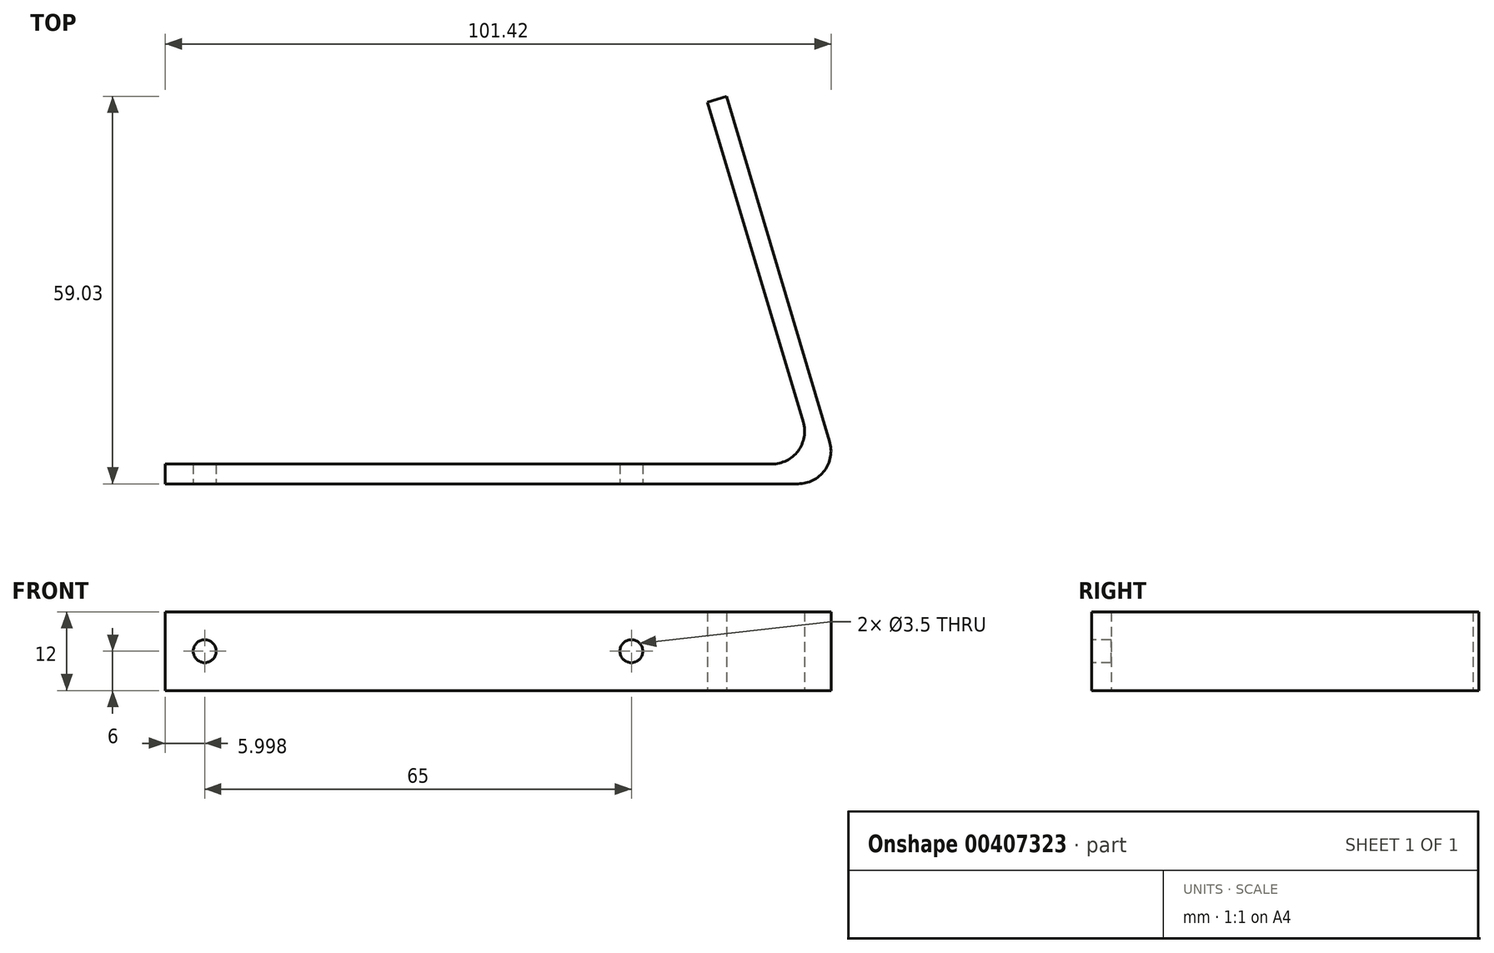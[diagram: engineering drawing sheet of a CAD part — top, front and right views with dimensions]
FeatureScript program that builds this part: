
annotation { "Feature Type Name" : "Feature", "Feature Type Description" : "" }
export const myFeature = defineFeature(function(context is Context, id is Id, definition is map)
    precondition{}
    {
        {
            var Q0;
            Q0=qCreatedBy(makeId("Top.planeOp"),FACE);
            var sketch = newSketch(context, id + "F0", { "sketchPlane" : qUnion([Q0])});
            skLineSegment(sketch, "E0.bottom", {"start": v(-64.62, -2.8) * mm, "end": v(27.77, -2.8) * mm});
            skLineSegment(sketch, "E0.top", {"start": v(-64.62, -5.8) * mm, "end": v(31.8, -5.8) * mm});
            skLineSegment(sketch, "E0.left", {"start": v(-64.62, -2.8) * mm, "end": v(-64.62, -5.8) * mm});
            skLineSegment(sketch, "E0.right", {"start": v(35.38, -2.8) * mm, "end": v(35.38, -5.8) * mm});
            skLineSegment(sketch, "E1", {"start": v(32.56, 3.64) * mm, "end": v(17.99, 52.37) * mm});
            skLineSegment(sketch, "E2", {"start": v(17.99, 52.37) * mm, "end": v(20.86, 53.23) * mm});
            skLineSegment(sketch, "E3", {"start": v(20.86, 53.23) * mm, "end": v(36.59, 0.64) * mm});
            skLineSegment(sketch, "E4", {"start": v(38.49, -5.72) * mm, "end": v(35.38, -5.8) * mm});
            skArc(sketch, "E5.filletArc", {"start": v(27.77, -2.8) * mm, "mid": v(31.78, -0.78) * mm, "end": v(32.56, 3.64) * mm});
            skArc(sketch, "E6.filletArc", {"start": v(31.8, -5.8) * mm, "mid": v(35.8, -3.78) * mm, "end": v(36.59, 0.64) * mm});
            skSolve(sketch);
        }
        {
            var Q0;
            Q0 = qSketchRegion(id + "F0", true);
            extrude(context, id + "F1", {"entities" : qUnion([Q0]), "depth" : 12 * mm});
        }
        {
            var Q0;
            Q0=makeQuery(id+"F1.opExtrude","SWEPT_FACE",FACE,{"disambiguationData":[OSD([sQuery(id+"F0.wireOp",EDGE,"E0.top")])]});
            var sketch = newSketch(context, id + "F2", { "sketchPlane" : qUnion([Q0])});
            skCircle(sketch, "E7", {"center": v(-58.62, 6) * mm, "radius": 1.75 * mm});
            skSolve(sketch);
        }
        {
            var Q0;
            Q0=makeQuery(id+"F2.imprint","IMPRINT",FACE,{"disambiguationData":[TD([[makeQuery(id+"F2.imprint","IMPRINT",EDGE,{"derivedFrom":sQuery(id+"F2.wireOp",EDGE,"E7")}),1.0]])]});
            extrude(context, id + "F3", {"entities" : qUnion([Q0]), "operationType" : NewBodyOperationType.REMOVE, "oppositeDirection" : true, "depth" : 25 * mm});
        }
        {
            var Q0;
            Q0=makeQuery(id+"F1.opExtrude","SWEPT_FACE",FACE,{"disambiguationData":[OSD([sQuery(id+"F0.wireOp",EDGE,"E0.top")])]});
            var sketch = newSketch(context, id + "F4", { "sketchPlane" : qUnion([Q0])});
            skCircle(sketch, "E8", {"center": v(6.38, 6) * mm, "radius": 1.75 * mm});
            skSolve(sketch);
        }
        {
            var Q0;
            Q0 = qSketchRegion(id + "F4", true);
            extrude(context, id + "F5", {"entities" : qUnion([Q0]), "operationType" : NewBodyOperationType.REMOVE, "oppositeDirection" : true, "depth" : 3 * mm});
        }
    });
